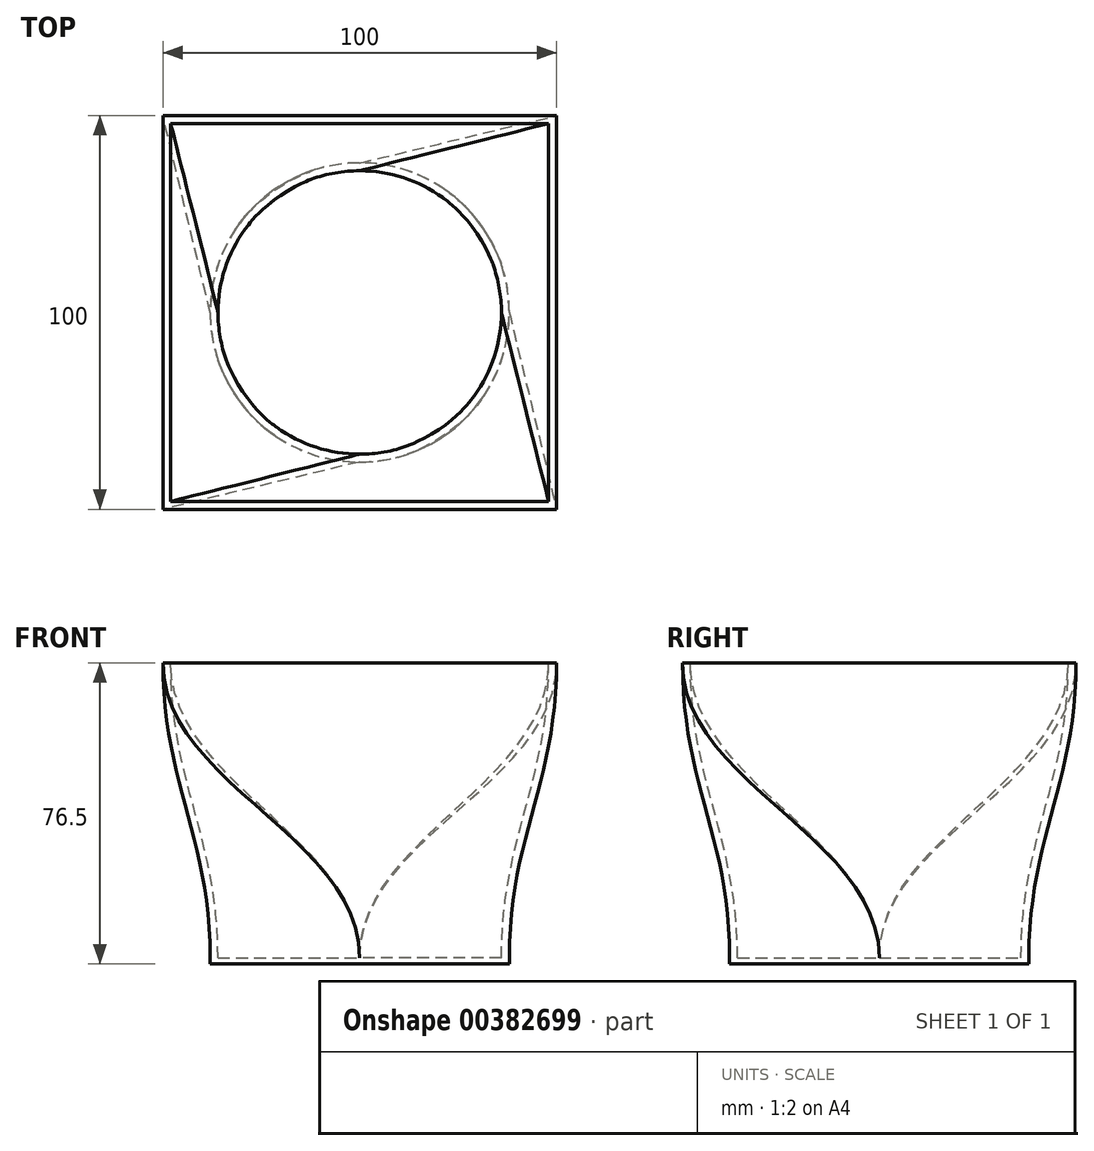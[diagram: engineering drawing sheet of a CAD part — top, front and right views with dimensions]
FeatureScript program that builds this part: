
annotation { "Feature Type Name" : "Feature", "Feature Type Description" : "" }
export const myFeature = defineFeature(function(context is Context, id is Id, definition is map)
    precondition{}
    {
        {
            var Q0;
            Q0=qCreatedBy(makeId("Top.planeOp"),FACE);
            var sketch = newSketch(context, id + "F0", { "sketchPlane" : qUnion([Q0])});
            skArc(sketch, "E0", {"start": v(0, 38) * mm, "mid": v(-26.87, 26.87) * mm, "end": v(-38, 0) * mm});
            skArc(sketch, "E1", {"start": v(38, 0) * mm, "mid": v(26.87, 26.87) * mm, "end": v(0, 38) * mm});
            skArc(sketch, "E2", {"start": v(0, -38) * mm, "mid": v(26.87, -26.87) * mm, "end": v(38, 0) * mm});
            skArc(sketch, "E3", {"start": v(-38, 0) * mm, "mid": v(-26.87, -26.87) * mm, "end": v(0, -38) * mm});
            skLineSegment(sketch, "E4", {"start": v(0, 43.63) * mm, "end": v(0, -49.53) * mm, "construction": true});
            skLineSegment(sketch, "E5", {"start": v(-43.23, 0) * mm, "end": v(48.32, 0) * mm, "construction": true});
            skSolve(sketch);
        }
        {
            var Q0;
            Q0=qCreatedBy(makeId("Top.planeOp"),FACE);
            cPlane(context, id + "F1", {"entities" : qUnion([Q0]), "cplaneType" : CPlaneType.OFFSET, "offset" : 75 * mm, "width" : 152.4 * mm, "height" : 152.4 * mm});
        }
        {
            var Q0;
            Q0=qCreatedBy(id+"F1.planeOp",FACE);
            var sketch = newSketch(context, id + "F2", { "sketchPlane" : qUnion([Q0])});
            skLineSegment(sketch, "E6.bottom", {"start": v(-50, 50) * mm, "end": v(50, 50) * mm});
            skLineSegment(sketch, "E6.top", {"start": v(-50, -50) * mm, "end": v(50, -50) * mm});
            skLineSegment(sketch, "E6.left", {"start": v(-50, 50) * mm, "end": v(-50, -50) * mm});
            skLineSegment(sketch, "E6.right", {"start": v(50, 50) * mm, "end": v(50, -50) * mm});
            skPoint(sketch, "E6.middle", {"position": v(0, 0) * mm});
            skSolve(sketch);
        }
        {
            var Q0;
            Q0=makeQuery(id+"F0.imprint","IMPRINT",FACE,{"disambiguationData":[TD([[makeQuery(id+"F0.imprint","IMPRINT",EDGE,{"derivedFrom":sQuery(id+"F0.wireOp",EDGE,"E0")}),1.0]])]});
            var Q1;
            Q1=makeQuery(id+"F2.imprint","IMPRINT",FACE,{"disambiguationData":[TD([[makeQuery(id+"F2.imprint","IMPRINT",EDGE,{"derivedFrom":sQuery(id+"F2.wireOp",EDGE,"E6.bottom")}),-1.0]])]});
            loft(context, id + "F3", {"startCondition" : LoftEndDerivativeType.NORMAL_TO_PROFILE, "startMagnitude" : 1.2, "endCondition" : LoftEndDerivativeType.NORMAL_TO_PROFILE, "endMagnitude" : 1.2, "sheetProfilesArray" : [{ "sheetProfileEntities" : qUnion([Q0]) }, { "sheetProfileEntities" : qUnion([Q1]) }]});
        }
        {
            var Q0;
            Q0=qCreatedBy(makeId("Top.planeOp"),FACE);
            var sketch = newSketch(context, id + "F4", { "sketchPlane" : qUnion([Q0])});
            skArc(sketch, "E7", {"start": v(0, 36) * mm, "mid": v(-25.46, 25.46) * mm, "end": v(-36, 0) * mm});
            skArc(sketch, "E8", {"start": v(36, 0) * mm, "mid": v(25.46, 25.46) * mm, "end": v(0, 36) * mm});
            skArc(sketch, "E9", {"start": v(0, -36) * mm, "mid": v(25.46, -25.46) * mm, "end": v(36, 0) * mm});
            skArc(sketch, "E10", {"start": v(-36, 0) * mm, "mid": v(-25.46, -25.46) * mm, "end": v(0, -36) * mm});
            skSolve(sketch);
        }
        {
            var Q0;
            Q0=makeQuery(id+"F2.imprint","IMPRINT",FACE,{"disambiguationData":[TD([[makeQuery(id+"F2.imprint","IMPRINT",EDGE,{"derivedFrom":sQuery(id+"F2.wireOp",EDGE,"E6.bottom")}),-1.0]])]});
            var sketch = newSketch(context, id + "F5", { "sketchPlane" : qUnion([Q0])});
            skLineSegment(sketch, "E11.bottom", {"start": v(-48, 48) * mm, "end": v(48, 48) * mm});
            skLineSegment(sketch, "E11.top", {"start": v(-48, -48) * mm, "end": v(48, -48) * mm});
            skLineSegment(sketch, "E11.left", {"start": v(-48, 48) * mm, "end": v(-48, -48) * mm});
            skLineSegment(sketch, "E11.right", {"start": v(48, 48) * mm, "end": v(48, -48) * mm});
            skPoint(sketch, "E11.middle", {"position": v(0, 0) * mm});
            skSolve(sketch);
        }
        {
            var Q0;
            Q0=qSketchRegion(id+"F4",true);
            var Q1;
            Q1=qSketchRegion(id+"F5",true);
            loft(context, id + "F6", {"operationType" : NewBodyOperationType.REMOVE, "startCondition" : LoftEndDerivativeType.NORMAL_TO_PROFILE, "startMagnitude" : 1.2, "endCondition" : LoftEndDerivativeType.NORMAL_TO_PROFILE, "endMagnitude" : 1.2, "sheetProfilesArray" : [{ "sheetProfileEntities" : qUnion([Q0]) }, { "sheetProfileEntities" : qUnion([Q1]) }]});
        }
        {
            var Q0;
            Q0=makeQuery(id+"F0.imprint","IMPRINT",FACE,{"disambiguationData":[TD([[makeQuery(id+"F0.imprint","IMPRINT",EDGE,{"derivedFrom":sQuery(id+"F0.wireOp",EDGE,"E0")}),1.0]])]});
            var Q1;
            Q1=makeQuery(id+"F4.imprint","IMPRINT",FACE,{"disambiguationData":[TD([[makeQuery(id+"F4.imprint","IMPRINT",EDGE,{"derivedFrom":sQuery(id+"F4.wireOp",EDGE,"E7")}),1.0]])]});
            extrude(context, id + "F7", {"entities" : qUnion([Q0, Q1]), "operationType" : NewBodyOperationType.ADD, "oppositeDirection" : true, "depth" : 1.5 * mm});
        }
    });
